# Revit family: MultiV+ R200G
name_source: partatom
category: Modelos genéricos
revit_build: Autodesk Revit 2017 (Build: 20170118_1100(x64)
units: mm (PartAtom-declared; Revit-internal decimal feet)

## family parameters
Compartido = No
Corte con vacíos al cargar = No
Cota de conector redondo = Diámetro de uso
Puede alojar armadura = No
Punto de cálculo de habitación = No
Tipo de pieza = Normal

## types (1)
- R200G01
    Altura = 220 mm  [stored 0.721785 ft]
    Anchura exterior = 236 mm
    Anchura interior = 200 mm  [stored 0.656168 ft]
    Caudal de referencia = 20 L/s
    Clase de carga = D-400 Norma EN-1433
    Costo = 83.83€
    Descripción = Canal de Hormigón Polímero tipo ULMA / modelo R200G / ancho exterior 236mm / ancho interior 200mm y con alturas exteriores disponibles entre 80mm y 370mm / con pendiente incorporada del 0.5% o pendiente en cascada / para recogida de aguas pluviales / sección en V optimizada con efecto autolimpiante / en módulos de 1 ML de longitud / fijación de seguridad en 8 puntos por ML / perfiles de acero galvanizado* para protección lateral / fijación sin tornillos RapidLock o atornillada
    Fabricante = ULMA Architectural
    Ficha técnica = http://www.ulmaarchitectural.com
    Modelo = R200G01
    Pendiente = 0.50%
    Peso = 29.58 kg
    Sección hidráulica = 294.60 cm²
    URL = http://www.ulmaarchitectural.com
    Ø salida horizontal = 0 mm
    Ø salida vertical = 160 mm

note: [stored X ft] marks values corroborated as IEEE doubles in the binary element streams (Revit-internal decimal feet)
